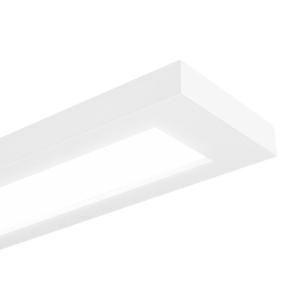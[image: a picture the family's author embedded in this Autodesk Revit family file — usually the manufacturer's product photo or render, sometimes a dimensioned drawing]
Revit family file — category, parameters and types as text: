
# Revit family: 3f_filippi_-_3f_travetta_op_3f_filippi_-_11513_-_3f_travetta_led_2x40w_dali_op_l2200
name_source: partatom
category: Lighting Fixtures
units: mm (PartAtom-declared; Revit-internal decimal feet)

## family parameters
Cut with Voids When Loaded = No
Host = Face
Light Source = No
Part Type = Normal
Room Calculation Point = No
Round Connector Dimension = Use Diameter
Shared = No

## types (1)
- 3F Filippi - 3F Travetta OP (1 x LED, 9511 lm, 90 W, 4000 K)
    Apparent Load = 90 VA
    Approval mark = ENEC
    CIE Flux Codes = 49 81 97 100 100
    Color Rendering = 80
    Color Temperature = 4000 K
    Control Gear = Electronic transformer
    Default Elevation = 1800 mm
    Description = ILLUMINOTECHNICAL
Luminous efficiency 100% (DLOR 100%, ULOR 0%).
Initial luminous flux of the luminaire 9511 lm.
Direct symmetric distribution.
Installation Interdistance Transv.D = 1.20 x hu - Long.D = 1.20 x hu.
Tabular UGR (CIE 117 - 4H-8H; S=0.25H; 70/50/20): RUG 23.9 - 24.7.
Beam angle: 104° - 107°.
Luminous efficacy 106 lm/W.
Lifetime (L93/B10): 30000 h. (tq+25°C)
Lifetime (L90/B10): 50000 h. (tq+25°C)
Lifetime (L85/B10): 80000 h. (tq+25°C)
Lifetime (L80/B10): 100000 h. (tq+25°C)
Sudden decreased luminous flux after 50000 hours: 0% (C0).
Photobiological safety in compliance with IEC/TR 62778: RG0 risk exempt, (IEC 62471).
In compliance with IEC/EN 62722-2-1 - IEC/EN 62717 standards.

SOURCE
2 linear LED modules 40W/840.
Energy efficiency class (UE 2019/2020 - UE 2019/2015): D.
CIE 13.3 Colour rendering index: CRI >80 (R9 <50%).
IES TM-30 Fidelity Index: Rf = 84 Rg = 95.
CCT nominal colour temperature 4000 K.
Colour initial tolerance (MacAdam): SDCM 3.

MECHANICAL
Housing with squared shape in white painted galvannealed steel, with nonreflecting surface.
Flow recuperator in semi-glossy aluminium.
Opal methacrylate (PMMA) flat diffuser, anti-glare.
Luminaire with limited surface temperature. - D - (EN 60598-2-24)
Dimensions: 2200x190 mm, height 60 mm (edge 40 mm). Weight 6.98 kg.
IP20 protection degree.
Glow-wire test resistance 650°C.

ELECTRICAL
Halogen Free DALI-2, PUSH-DIM, electronic wiring 230V-50/60Hz, power factor 0.95 at full load, THD <25%, constant output current, SELV, class I, 2 driver, 2 DALI addresses.
Power of the luminaire 90 W.
CE - IEC 60598-1 - EN 60598-1.
SAFE FLICKER: PstLM=<1 and SVM=<0.4 (IEC TR 61547-1 and IEC TR 63158), to ensure a more comfortable and safe light.
Luminaire compliant with EN 60598-2-22 for power supply from a centralised emergency system CPSS (Central Power Supply System), not incorporated in the luminaire - high risk areas excluded. The default power and flux are 100% in AC and 15% in DC.
Ambient temperature from 0°C to +25°C.
Temperature class T6 max 85°C.
Relative humidity UR: <85%.

INSTALLATION
Ceiling / Suspended.
All accessories dedicated to this product are available on the Catalog and on our website www.3F-Filippi.com.

APPLICATIONS
In environments, even with reduced height, requiring a comfortable light.
Exhibitions area, halls, great halls and shops.

LIGHT MANAGEMENT
Recommended minimum setting: 10%.
The device, equipped with DALI-2 driver, can be controlled manually with 3F Easy Dim technology or automatically/manually with 3F Smart Dimming technology and/or centralised DALI systems.
DALI-2 certification guarantees interoperability with other devices with the same certification.
In electrical systems without a regulation system (manual or automatic) and DALI bus, a suitable jumper must be made on the DA-DA terminals of the appliance.

WARNING
Luminaire designed for disposal/recycling at end-of-life.
Replaceable (LED only) light source by a professional. Replaceable control gear by a professional.
    Height = 60 mm  [stored 0.19685 ft]
    Lamp = 1 x LED
    Lamp Light Flux = 9511 lm
    Lamp Power = 90 W
    Lamp count = 1
    Length = 2200 mm
    Lifetime = 50000 h
    Luminous efficacy = 106 lm/W
    Manufacturer = 3F Filippi
    ModVariant = No
    Model = 3F Filippi - 11513 - 3F Travetta LED 2x40W DALI OP L2200
    Mounting Place = Ceiling
    Mounting Type = Pendant
    Number of Poles = 1
    OnlyDefault = Yes
    Power Factor = 1
    Product Name = 3F Filippi - 3F Travetta OP
    Product group = pendant luminaire
    ProductGroupID = 9
    Protection Class = Protection class I
    Protection Degree = IP 20
    RLX_Detail_Level = 1
    RLX_Emergency_Light_Flux = 0 lm
    RLX_Emergency_Type = 0
    RLX_Emergency_Type_DB = No
    RlxData = <blob elided: 37673 chars, md5=ac20a7d9>
    Socket = socket
    Standby Power = 0 W
    System Light Flux = 9511 lm
    System Power = 90 W
    Type Comments = Product without accessories
    Type Image = 3ffilippi_3f_travetta_led_op.jpg
    URL = http://relux.com
    VarID = ---
    Voltage = 0 V
    Weight = 0.00 kg
    Width = 190 mm  [stored 0.62336 ft]

note: [stored X ft] marks values corroborated as IEEE doubles in the binary element streams (Revit-internal decimal feet)

## geometry (parser evidence)
native form markers: Blend x4, Sweep x12
no freeform markers — native parametric forms only
